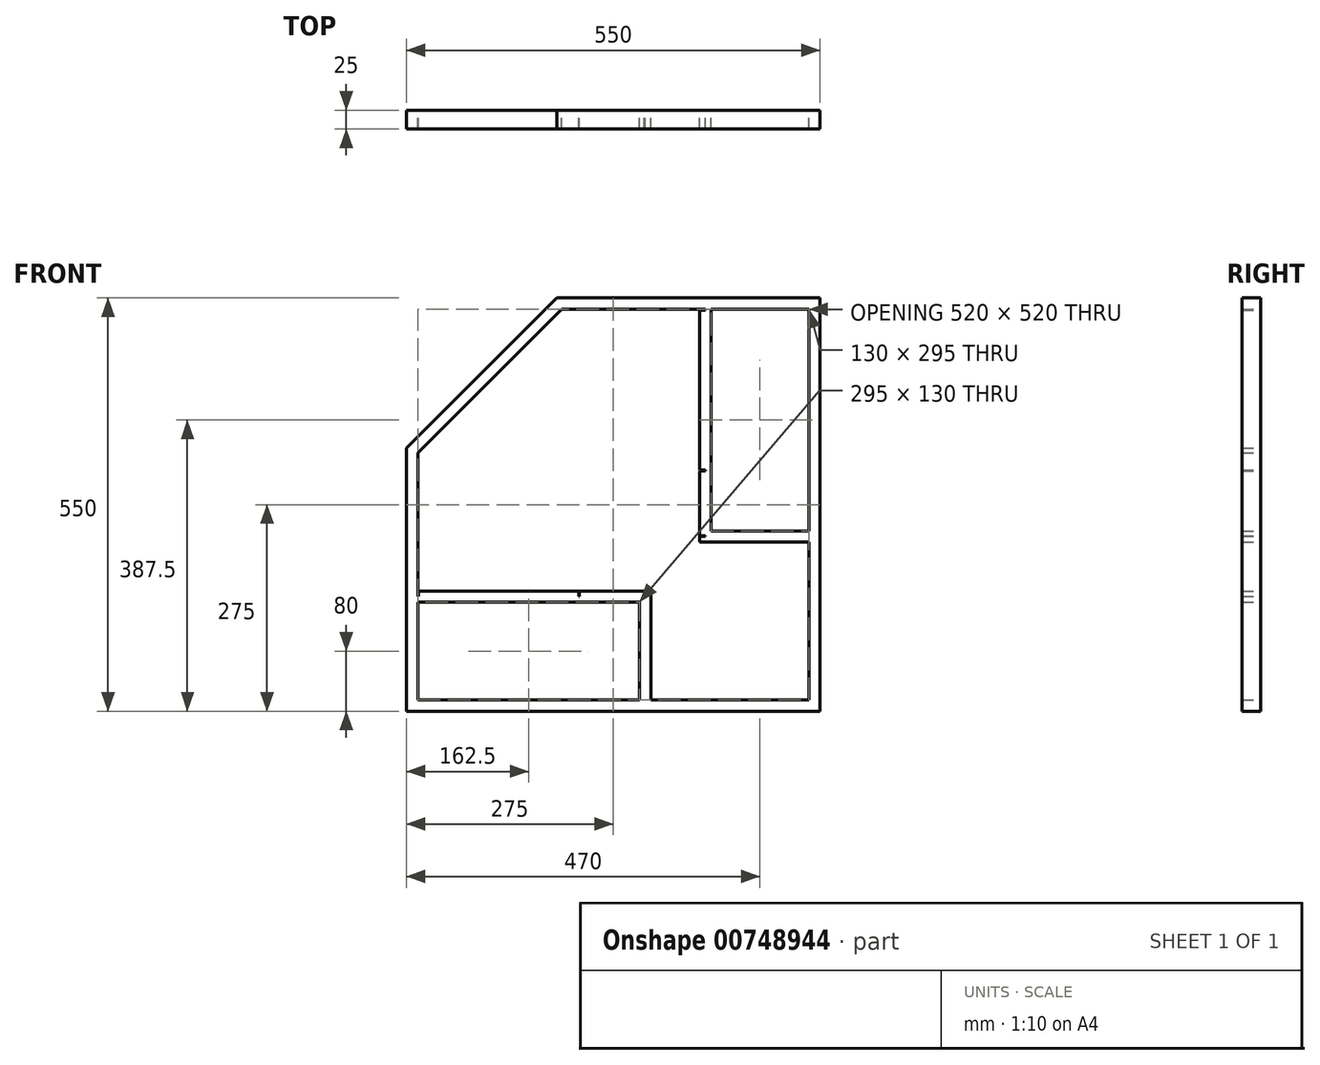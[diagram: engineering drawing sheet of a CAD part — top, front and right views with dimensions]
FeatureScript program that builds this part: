
annotation { "Feature Type Name" : "Feature", "Feature Type Description" : "" }
export const myFeature = defineFeature(function(context is Context, id is Id, definition is map)
    precondition{}
    {
        {
            var Q0;
            Q0=qCreatedBy(makeId("Front.planeOp"),FACE);
            var sketch = newSketch(context, id + "F0", { "sketchPlane" : qUnion([Q0])});
            skLineSegment(sketch, "E0.top", {"start": v(-275, -275) * mm, "end": v(275, -275) * mm});
            skLineSegment(sketch, "E0.right", {"start": v(275, 275) * mm, "end": v(275, -275) * mm});
            skPoint(sketch, "E0.middle", {"position": v(0, 0) * mm});
            skLineSegment(sketch, "E1", {"start": v(-75, 275) * mm, "end": v(275, 275) * mm});
            skLineSegment(sketch, "E2", {"start": v(-275, -275) * mm, "end": v(-275, 75) * mm});
            skLineSegment(sketch, "E3", {"start": v(275, 275) * mm, "end": v(-75, 275) * mm});
            skLineSegment(sketch, "E4", {"start": v(-75, 275) * mm, "end": v(-275, 75) * mm});
            skPoint(sketch, "E5.orphan", {"position": v(-275, 275) * mm});
            skLineSegment(sketch, "E6.0", {"start": v(-260, -260) * mm, "end": v(-260, -130) * mm});
            skLineSegment(sketch, "E6.1", {"start": v(-68.79, 260) * mm, "end": v(-260, 68.79) * mm});
            skLineSegment(sketch, "E6.2", {"start": v(-260, -260) * mm, "end": v(35, -260) * mm});
            skLineSegment(sketch, "E6.3", {"start": v(260, 260) * mm, "end": v(260, -35) * mm});
            skLineSegment(sketch, "E6.4", {"start": v(260, 260) * mm, "end": v(130, 260) * mm});
            skLineSegment(sketch, "E7", {"start": v(-275, 275) * mm, "end": v(-175, 175) * mm, "construction": true});
            skLineSegment(sketch, "E8.trimOffspring", {"start": v(275, -275) * mm, "end": v(391.98, -391.98) * mm, "construction": true});
            skLineSegment(sketch, "E9", {"start": v(260, -260) * mm, "end": v(47.8, -47.8) * mm, "construction": true});
            skCircle(sketch, "E10", {"center": v(153.9, -153.9) * mm, "radius": 65 * mm});
            skCircle(sketch, "E11", {"center": v(-58.3, 58.3) * mm, "radius": 65 * mm, "construction": true});
            skLineSegment(sketch, "E12.bottom", {"start": v(260, -50) * mm, "end": v(267.5, -50) * mm});
            skLineSegment(sketch, "E12.top", {"start": v(260, -35) * mm, "end": v(267.5, -35) * mm});
            skLineSegment(sketch, "E12.right", {"start": v(267.5, -50) * mm, "end": v(267.5, -35) * mm});
            skLineSegment(sketch, "E13.trimOffspring", {"start": v(260, -50) * mm, "end": v(260, -260) * mm});
            skLineSegment(sketch, "E14", {"start": v(260, -35) * mm, "end": v(130, -35) * mm});
            skLineSegment(sketch, "E15", {"start": v(130, 260) * mm, "end": v(130, -35) * mm});
            skLineSegment(sketch, "E16.0", {"start": v(260, -50) * mm, "end": v(115, -50) * mm});
            skLineSegment(sketch, "E17.MirrorCS", {"start": v(-258.59, -115) * mm, "end": v(-46, -115) * mm});
            skLineSegment(sketch, "E18.MirrorCS", {"start": v(-260, -130) * mm, "end": v(35, -130) * mm});
            skLineSegment(sketch, "E19.MirrorCS", {"start": v(50, -260) * mm, "end": v(50, -115) * mm});
            skLineSegment(sketch, "E20.MirrorCS", {"start": v(35, -260) * mm, "end": v(35, -130) * mm});
            skLineSegment(sketch, "E21.MirrorCS", {"start": v(35, -260) * mm, "end": v(35, -267.5) * mm});
            skLineSegment(sketch, "E22.MirrorCS", {"start": v(50, -260) * mm, "end": v(50, -267.5) * mm});
            skLineSegment(sketch, "E23.MirrorCS", {"start": v(50, -267.5) * mm, "end": v(35, -267.5) * mm});
            skLineSegment(sketch, "E24.trimOffspring", {"start": v(50, -260) * mm, "end": v(260, -260) * mm});
            skLineSegment(sketch, "E25.bottom", {"start": v(-260, -130) * mm, "end": v(-267.5, -130) * mm});
            skLineSegment(sketch, "E25.top", {"start": v(-260, -115) * mm, "end": v(-267.5, -115) * mm});
            skLineSegment(sketch, "E25.right", {"start": v(-267.5, -130) * mm, "end": v(-267.5, -115) * mm});
            skLineSegment(sketch, "E26.trimOffspring", {"start": v(-260, -115) * mm, "end": v(-260, 68.79) * mm});
            skLineSegment(sketch, "E27.top", {"start": v(130, 267.5) * mm, "end": v(115, 267.5) * mm});
            skLineSegment(sketch, "E27.left", {"start": v(130, 260) * mm, "end": v(130, 267.5) * mm});
            skLineSegment(sketch, "E27.right", {"start": v(115, 260) * mm, "end": v(115, 267.5) * mm});
            skLineSegment(sketch, "E28.trimOffspring", {"start": v(115, 260) * mm, "end": v(-68.79, 260) * mm});
            skLineSegment(sketch, "E29", {"start": v(-260, -115) * mm, "end": v(-260, -122.5) * mm});
            skLineSegment(sketch, "E30", {"start": v(115, 260) * mm, "end": v(122.5, 260) * mm});
            skLineSegment(sketch, "E31", {"start": v(122.5, 259) * mm, "end": v(122.5, 260) * mm});
            skLineSegment(sketch, "E32.0", {"start": v(-259, -115.41) * mm, "end": v(-259, -122.5) * mm});
            skLineSegment(sketch, "E32.2", {"start": v(115.41, 259) * mm, "end": v(122.5, 259) * mm});
            skLineSegment(sketch, "E33.trimOffspring", {"start": v(-44.33, -115) * mm, "end": v(39.4, -115) * mm});
            skLineSegment(sketch, "E34", {"start": v(-260, -122.5) * mm, "end": v(-259, -122.5) * mm});
            skLineSegment(sketch, "E35", {"start": v(50, -115) * mm, "end": v(42.5, -115) * mm});
            skLineSegment(sketch, "E36", {"start": v(42.5, -115) * mm, "end": v(42.5, -122.5) * mm});
            skLineSegment(sketch, "E37", {"start": v(42.5, -122.5) * mm, "end": v(41.5, -122.5) * mm});
            skLineSegment(sketch, "E38", {"start": v(41.5, -122.5) * mm, "end": v(41.5, -115) * mm});
            skLineSegment(sketch, "E39", {"start": v(39.4, -115) * mm, "end": v(41.5, -115) * mm});
            skLineSegment(sketch, "E40.MirrorCS", {"start": v(122.5, -41.5) * mm, "end": v(115, -41.5) * mm});
            skLineSegment(sketch, "E41.MirrorCS", {"start": v(122.5, -42.5) * mm, "end": v(122.5, -41.5) * mm});
            skLineSegment(sketch, "E42.MirrorCS", {"start": v(115, -42.5) * mm, "end": v(122.5, -42.5) * mm});
            skLineSegment(sketch, "E43", {"start": v(115, -50) * mm, "end": v(115, -42.5) * mm});
            skLineSegment(sketch, "E44", {"start": v(50, -115) * mm, "end": v(-45, -115) * mm});
            skLineSegment(sketch, "E45", {"start": v(-45, -115) * mm, "end": v(-45, -122.5) * mm});
            skLineSegment(sketch, "E46", {"start": v(-45, -122.5) * mm, "end": v(-46, -122.5) * mm});
            skLineSegment(sketch, "E47", {"start": v(-46, -122.5) * mm, "end": v(-46, -115) * mm});
            skPoint(sketch, "E48.orphan", {"position": v(-46, -115) * mm});
            skLineSegment(sketch, "E49.MirrorCS", {"start": v(122.5, 45) * mm, "end": v(122.5, 46) * mm});
            skLineSegment(sketch, "E50.MirrorCS", {"start": v(122.5, 46) * mm, "end": v(115, 46) * mm});
            skLineSegment(sketch, "E51.MirrorCS", {"start": v(115, 45) * mm, "end": v(122.5, 45) * mm});
            skLineSegment(sketch, "E52.trimOffspring", {"start": v(115, 46) * mm, "end": v(115, 258.59) * mm});
            skLineSegment(sketch, "E53", {"start": v(115, -41.5) * mm, "end": v(115, 45) * mm});
            skLineSegment(sketch, "E54", {"start": v(115, 258.59) * mm, "end": v(115, 259) * mm});
            skLineSegment(sketch, "E55", {"start": v(115.41, 259) * mm, "end": v(115, 259) * mm});
            skLineSegment(sketch, "E56.MirrorCS", {"start": v(-258.59, -115) * mm, "end": v(-259, -115) * mm});
            skLineSegment(sketch, "E57.MirrorCS", {"start": v(-259, -115.41) * mm, "end": v(-259, -115) * mm});
            skLineSegment(sketch, "E58", {"start": v(275, -275) * mm, "end": v(386.96, -163.04) * mm});
            skLineSegment(sketch, "E59", {"start": v(-260, 68.79) * mm, "end": v(-275, 75) * mm});
            skLineSegment(sketch, "E60", {"start": v(-68.79, 260) * mm, "end": v(-75, 275) * mm});
            skLineSegment(sketch, "E61", {"start": v(-260, 68.79) * mm, "end": v(-268.73, 60.06) * mm});
            skPoint(sketch, "E61.endSnap0", {"position": v(-260.06, 60.06) * mm});
            skLineSegment(sketch, "E62", {"start": v(-268.73, 60.06) * mm, "end": v(-275, 53.79) * mm});
            skLineSegment(sketch, "E63", {"start": v(-68.79, 260) * mm, "end": v(-79.4, 270.6) * mm});
            skLineSegment(sketch, "E64", {"start": v(-260, 68.79) * mm, "end": v(-275, 68.79) * mm});
            skPoint(sketch, "E65.start.orphan", {"position": v(-260, 75) * mm});
            skLineSegment(sketch, "E66", {"start": v(-68.79, 260) * mm, "end": v(-68.79, 275) * mm});
            skLineSegment(sketch, "E67", {"start": v(-45, -115) * mm, "end": v(115, 45) * mm});
            skLineSegment(sketch, "E68", {"start": v(-259, -115) * mm, "end": v(115, 259) * mm});
            skSolve(sketch);
        }
        {
            var Q0;
            Q0 = qSketchRegion(id + "F0", true);
            var Q1;
            Q1=makeQuery(id+"F0.imprint","IMPRINT",FACE,{"disambiguationData":[TD([[makeQuery(id+"F0.imprint","IMPRINT",EDGE,{"derivedFrom":sQuery(id+"F0.wireOp",EDGE,"E17.MirrorCS")}),-1.0]])]});
            var Q2;
            Q2=makeQuery(id+"F0.imprint","IMPRINT",FACE,{"disambiguationData":[TD([[makeQuery(id+"F0.imprint","IMPRINT",EDGE,{"derivedFrom":sQuery(id+"F0.wireOp",EDGE,"E12.bottom")}),1.0]])]});
            extrude(context, id + "F1", {"entities" : qUnion([Q0, Q1, Q2]), "depth" : 25 * mm, "offsetDistance" : 25 * mm});
        }
    });
